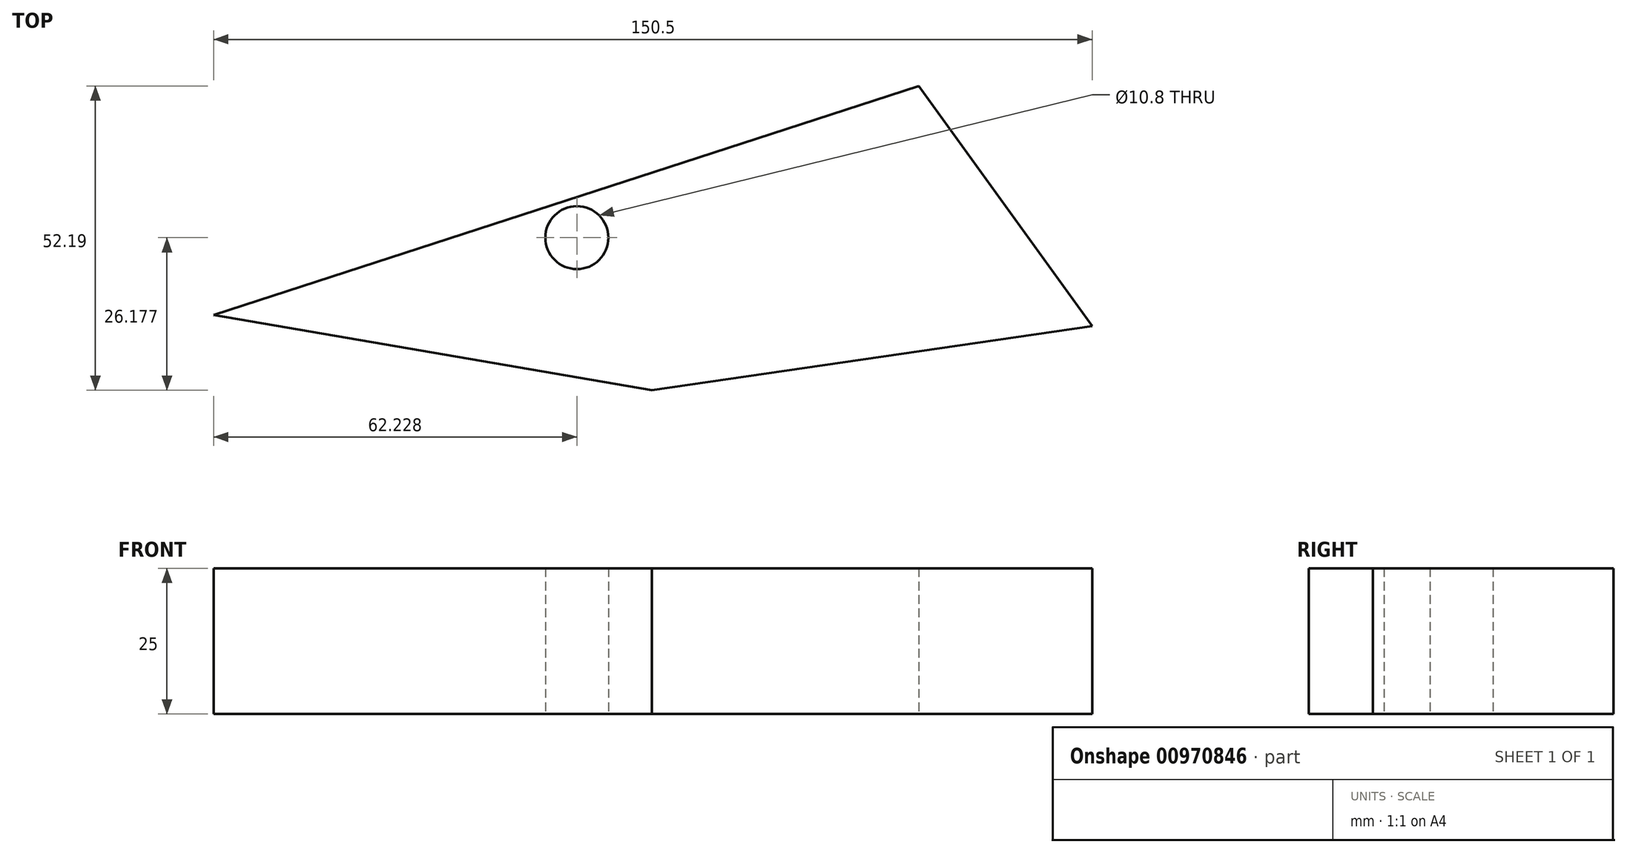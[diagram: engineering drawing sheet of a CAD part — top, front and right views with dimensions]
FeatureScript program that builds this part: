
annotation { "Feature Type Name" : "Feature", "Feature Type Description" : "" }
export const myFeature = defineFeature(function(context is Context, id is Id, definition is map)
    precondition{}
    {
        {
            var Q0;
            Q0=qCreatedBy(makeId("Top.planeOp"),FACE);
            var sketch = newSketch(context, id + "F0", { "sketchPlane" : qUnion([Q0])});
            skLineSegment(sketch, "E0", {"start": v(-83.89, 0) * mm, "end": v(36.89, 39.28) * mm});
            skLineSegment(sketch, "E1", {"start": v(36.89, 39.28) * mm, "end": v(66.61, -1.91) * mm});
            skLineSegment(sketch, "E2", {"start": v(66.61, -1.91) * mm, "end": v(-8.79, -12.9) * mm});
            skLineSegment(sketch, "E3", {"start": v(-83.89, 0) * mm, "end": v(-8.79, -12.9) * mm});
            skCircle(sketch, "E4", {"center": v(-21.66, 13.27) * mm, "radius": 5.4 * mm});
            skSolve(sketch);
        }
        {
            var Q0;
            Q0=makeQuery(id+"F0.imprint","IMPRINT",FACE,{"disambiguationData":[TD([[makeQuery(id+"F0.imprint","IMPRINT",EDGE,{"derivedFrom":sQuery(id+"F0.wireOp",EDGE,"E0")}),-1.0]])]});
            extrude(context, id + "F1", {"entities" : qUnion([Q0]), "depth" : 25 * mm, "offsetDistance" : 25 * mm});
        }
    });
